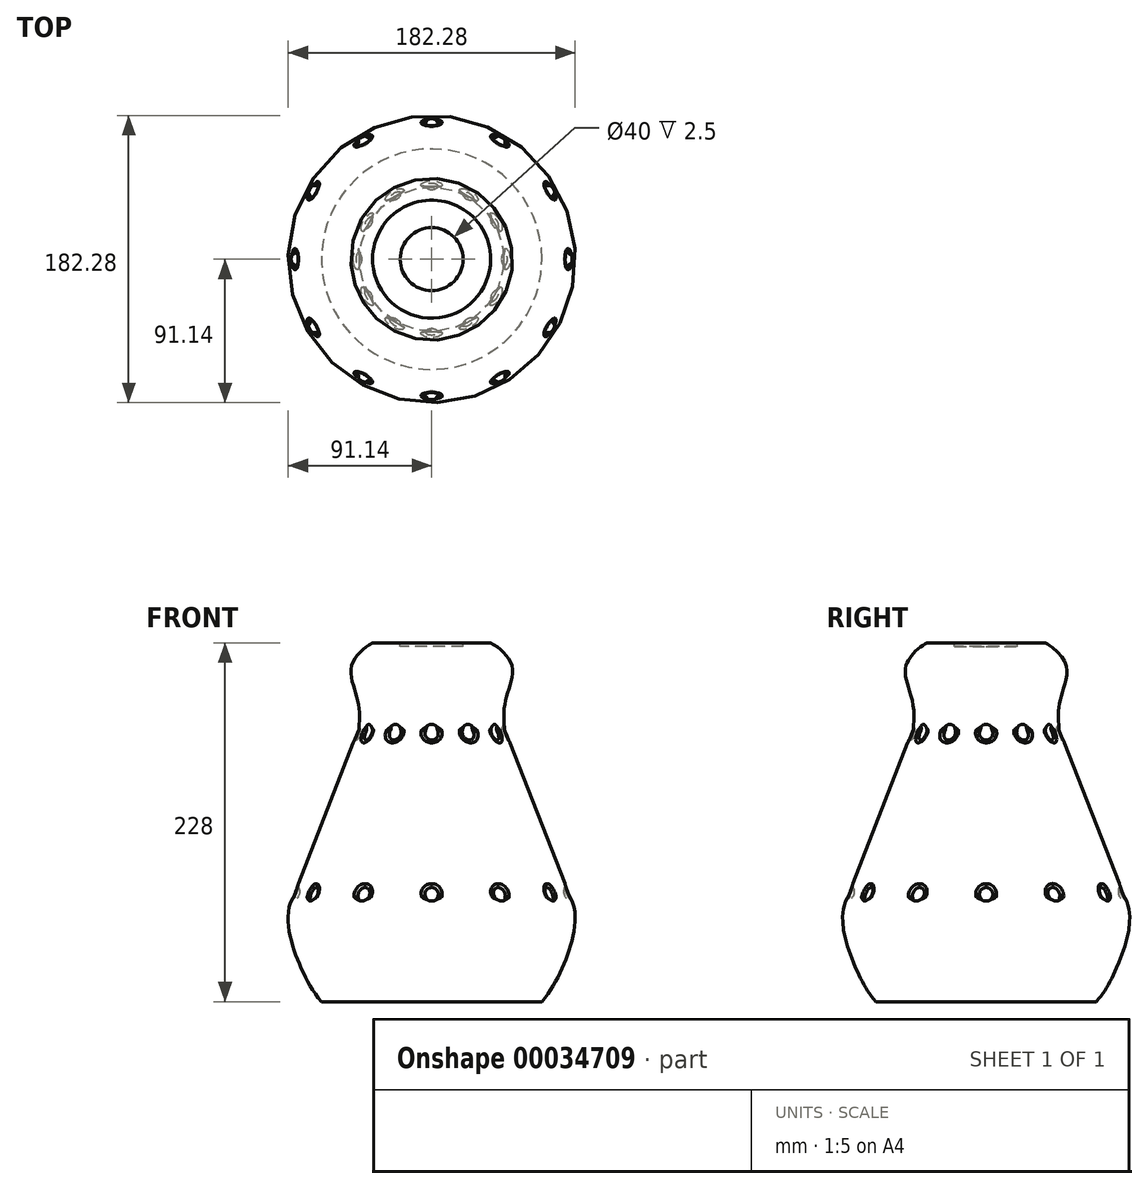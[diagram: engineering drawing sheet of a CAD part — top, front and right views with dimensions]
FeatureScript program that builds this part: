
annotation { "Feature Type Name" : "Feature", "Feature Type Description" : "" }
export const myFeature = defineFeature(function(context is Context, id is Id, definition is map)
    precondition{}
    {
        {
            var Q0;
            Q0=qCreatedBy(makeId("Front.planeOp"),FACE);
            var sketch = newSketch(context, id + "F0", { "sketchPlane" : qUnion([Q0])});
            skLineSegment(sketch, "E0", {"start": v(0, 0) * mm, "end": v(-70, 0) * mm});
            skLineSegment(sketch, "E1", {"start": v(0, 228) * mm, "end": v(-37.5, 228) * mm});
            skLineSegment(sketch, "E2", {"start": v(0, 228) * mm, "end": v(0, 0) * mm});
            skLineSegment(sketch, "E3", {"start": v(-46.67, 172.62) * mm, "end": v(-88.05, 66.08) * mm});
            skFitSpline(sketch, "E4", {"points": [v(-88.05, 66.08) * mm, v(-90.11, 61.28) * mm, v(-89.71, 41.07) * mm, v(-70, 0) * mm], "startDerivative": vector(-11.67, -20.15) * mm, "endDerivative": vector(46.37, -50.31) * mm});
            skFitSpline(sketch, "E5", {"points": [v(-46.67, 172.62) * mm, v(-46.67, 190.1) * mm, v(-50.97, 213.18) * mm, v(-37.5, 228) * mm], "startDerivative": vector(7.32, 26.53) * mm, "endDerivative": vector(45.51, 25.13) * mm});
            skSolve(sketch);
        }
        {
            var Q0;
            Q0=makeQuery(id+"F0.imprint","IMPRINT",FACE,{"disambiguationData":[TD([[makeQuery(id+"F0.imprint","IMPRINT",EDGE,{"derivedFrom":sQuery(id+"F0.wireOp",EDGE,"E0")}),-1.0]])]});
            var Q1;
            Q1=sQuery(id+"F0.wireOp",EDGE,"E2");
            revolve(context, id + "F1", {"entities" : qUnion([Q0]), "axis" : qUnion([Q1]), "revolveType" : RevolveType.FULL});
        }
        {
            var Q0;
            Q0=qCreatedBy(makeId("Right.planeOp"),FACE);
            var Q1;
            Q1=sQuery(id+"F0.wireOp",EDGE,"E3");
            cPlane(context, id + "F2", {"entities" : qUnion([Q0, Q1]), "cplaneType" : CPlaneType.LINE_ANGLE, "offset" : 150 * mm, "angle" : 0 * degree, "width" : 150 * mm, "height" : 150 * mm});
        }
        {
            var Q0;
            Q0=qCreatedBy(id+"F2.planeOp",FACE);
            cPlane(context, id + "F3", {"entities" : qUnion([Q0]), "cplaneType" : CPlaneType.OFFSET, "offset" : 3 * mm, "width" : 150 * mm, "height" : 150 * mm});
        }
        {
            var Q0;
            Q0=qCreatedBy(id+"F3.planeOp",FACE);
            var sketch = newSketch(context, id + "F4", { "sketchPlane" : qUnion([Q0])});
            skLineSegment(sketch, "E6.bottom", {"start": v(0, 141.96) * mm, "end": v(0, 141.96) * mm});
            skLineSegment(sketch, "E6.top", {"start": v(0, 31.96) * mm, "end": v(0, 31.96) * mm});
            skLineSegment(sketch, "E6.left", {"start": v(0, 141.96) * mm, "end": v(0, 31.96) * mm});
            skLineSegment(sketch, "E6.right", {"start": v(0, 141.96) * mm, "end": v(0, 31.96) * mm});
            skCircle(sketch, "E7", {"center": v(0, 141.96) * mm, "radius": 6 * mm});
            skLineSegment(sketch, "E8", {"start": v(0, 141.96) * mm, "end": v(0, 147.96) * mm});
            skCircle(sketch, "E9.1.0.0", {"center": v(0, 120.09) * mm, "radius": 6 * mm});
            skCircle(sketch, "E9.2.0.0", {"center": v(-0.02, 98.21) * mm, "radius": 6 * mm});
            skCircle(sketch, "E9.3.0.0", {"center": v(-0.03, 76.34) * mm, "radius": 6 * mm});
            skCircle(sketch, "E9.4.0.0", {"center": v(-0.04, 54.47) * mm, "radius": 6 * mm});
            skCircle(sketch, "E9.5.0.0", {"center": v(-0.05, 32.6) * mm, "radius": 6 * mm});
            skLineSegment(sketch, "E9.direction1", {"start": v(0, 141.96) * mm, "end": v(0, 120.09) * mm, "construction": true});
            skLineSegment(sketch, "E10", {"start": v(0, 31.96) * mm, "end": v(0, 26.6) * mm});
            skSolve(sketch);
        }
        {
            var Q0;
            {var subQ0=sQuery(id+"F4.wireOp",EDGE,"E8");Q0=makeQuery(id+"F4.imprint","IMPRINT",FACE,{"disambiguationData":[TD([[makeQuery(id+"F4.imprint","IMPRINT",EDGE,{"derivedFrom":subQ0}),-1.0]])]});}
            var Q1;
            {var subQ0=sQuery(id+"F4.wireOp",EDGE,"E9.1.0.0");var subQ1=sQuery(id+"F4.wireOp",EDGE,"E6.right");var subQ2=makeQuery(id+"F4.imprint","INTERSECT",VERTEX,{"disambiguationData":[OD(0.0)],"derivedFrom":[subQ1,subQ0]});Q1=makeQuery(id+"F4.imprint","IMPRINT",FACE,{"disambiguationData":[TD([[makeQuery(id+"F4.imprint","IMPRINT",EDGE,{"disambiguationData":[TD([[subQ2,1.0]])],"derivedFrom":subQ1}),1.0]])]});}
            var Q2;
            {var subQ0=sQuery(id+"F4.wireOp",EDGE,"E9.2.0.0");var subQ1=sQuery(id+"F4.wireOp",EDGE,"E6.right");var subQ2=makeQuery(id+"F4.imprint","INTERSECT",VERTEX,{"disambiguationData":[OD(0.0)],"derivedFrom":[subQ1,subQ0]});Q2=makeQuery(id+"F4.imprint","IMPRINT",FACE,{"disambiguationData":[TD([[makeQuery(id+"F4.imprint","IMPRINT",EDGE,{"disambiguationData":[TD([[subQ2,1.0]])],"derivedFrom":subQ1}),1.0]])]});}
            var Q3;
            {var subQ0=sQuery(id+"F4.wireOp",EDGE,"E9.3.0.0");var subQ1=sQuery(id+"F4.wireOp",EDGE,"E6.right");var subQ2=makeQuery(id+"F4.imprint","INTERSECT",VERTEX,{"disambiguationData":[OD(0.0)],"derivedFrom":[subQ1,subQ0]});Q3=makeQuery(id+"F4.imprint","IMPRINT",FACE,{"disambiguationData":[TD([[makeQuery(id+"F4.imprint","IMPRINT",EDGE,{"disambiguationData":[TD([[subQ2,1.0]])],"derivedFrom":subQ1}),1.0]])]});}
            var Q4;
            {var subQ0=sQuery(id+"F4.wireOp",EDGE,"E9.4.0.0");var subQ1=sQuery(id+"F4.wireOp",EDGE,"E6.right");var subQ2=makeQuery(id+"F4.imprint","INTERSECT",VERTEX,{"disambiguationData":[OD(0.0)],"derivedFrom":[subQ1,subQ0]});Q4=makeQuery(id+"F4.imprint","IMPRINT",FACE,{"disambiguationData":[TD([[makeQuery(id+"F4.imprint","IMPRINT",EDGE,{"disambiguationData":[TD([[subQ2,1.0]])],"derivedFrom":subQ1}),1.0]])]});}
            var Q5;
            {var subQ0=sQuery(id+"F4.wireOp",EDGE,"E10");Q5=makeQuery(id+"F4.imprint","IMPRINT",FACE,{"disambiguationData":[TD([[makeQuery(id+"F4.imprint","IMPRINT",EDGE,{"derivedFrom":subQ0}),1.0]])]});}
            var Q6;
            Q6=sQuery(id+"F4.wireOp",EDGE,"E6.right");
            revolve(context, id + "F5", {"entities" : qUnion([Q0, Q1, Q2, Q3, Q4, Q5]), "axis" : qUnion([Q6]), "revolveType" : RevolveType.FULL, "oppositeDirection" : true});
        }
        {
            var Q0;
            Q0=makeQuery(id+"F5.opRevolve","SWEPT_BODY",BODY,{"disambiguationData":[OSD([sQuery(id+"F4.wireOp",EDGE,"E6.right"),sQuery(id+"F4.wireOp",EDGE,"E7"),sQuery(id+"F4.wireOp",EDGE,"E8")])]});
            var Q1;
            Q1=makeQuery(id+"F5.opRevolve","SWEPT_BODY",BODY,{"disambiguationData":[OSD([sQuery(id+"F4.wireOp",EDGE,"E6.right"),sQuery(id+"F4.wireOp",EDGE,"E9.1.0.0")])]});
            var Q2;
            Q2=makeQuery(id+"F5.opRevolve","SWEPT_BODY",BODY,{"disambiguationData":[OSD([sQuery(id+"F4.wireOp",EDGE,"E6.right"),sQuery(id+"F4.wireOp",EDGE,"E9.2.0.0")])]});
            var Q3;
            Q3=makeQuery(id+"F5.opRevolve","SWEPT_BODY",BODY,{"disambiguationData":[OSD([sQuery(id+"F4.wireOp",EDGE,"E6.right"),sQuery(id+"F4.wireOp",EDGE,"E9.3.0.0")])]});
            var Q4;
            Q4=makeQuery(id+"F5.opRevolve","SWEPT_BODY",BODY,{"disambiguationData":[OSD([sQuery(id+"F4.wireOp",EDGE,"E6.right"),sQuery(id+"F4.wireOp",EDGE,"E9.4.0.0")])]});
            var Q5;
            Q5=makeQuery(id+"F5.opRevolve","SWEPT_BODY",BODY,{"disambiguationData":[OSD([sQuery(id+"F4.wireOp",EDGE,"E6.right"),sQuery(id+"F4.wireOp",EDGE,"E9.5.0.0"),sQuery(id+"F4.wireOp",EDGE,"E10")])]});
            var Q6;
            Q6=sQuery(id+"F0.wireOp",EDGE,"E2");
            circularPattern(context, id + "F6", {"operationType" : NewBodyOperationType.REMOVE, "entities" : qUnion([Q0, Q1, Q2, Q3, Q4, Q5]), "axis" : qUnion([Q6]), "angle" : 30 * degree, "instanceCount" : 12});
        }
        {
            var Q0;
            Q0=makeQuery(id+"F1.opRevolve","SWEPT_FACE",FACE,{"disambiguationData":[OSD([sQuery(id+"F0.wireOp",EDGE,"E3")])]});
            fillet(context, id + "F7", {"entities" : qUnion([Q0]), "radius" : 3 * mm, "tangentPropagation" : true, "allowEdgeOverflow" : false});
        }
        {
            var Q0;
            Q0=makeQuery(id+"F1.opRevolve","SWEPT_FACE",FACE,{"disambiguationData":[OSD([sQuery(id+"F0.wireOp",EDGE,"E1")])]});
            var sketch = newSketch(context, id + "F8", { "sketchPlane" : qUnion([Q0])});
            skCircle(sketch, "E11", {"center": v(0, 0) * mm, "radius": 20 * mm});
            skSolve(sketch);
        }
        {
            var Q0;
            Q0=makeQuery(id+"F8.imprint","IMPRINT",FACE,{"disambiguationData":[TD([[makeQuery(id+"F8.imprint","IMPRINT",EDGE,{"derivedFrom":sQuery(id+"F8.wireOp",EDGE,"E11")}),1.0]])]});
            extrude(context, id + "F9", {"entities" : qUnion([Q0]), "operationType" : NewBodyOperationType.REMOVE, "oppositeDirection" : true, "depth" : 2.5 * mm});
        }
    });
